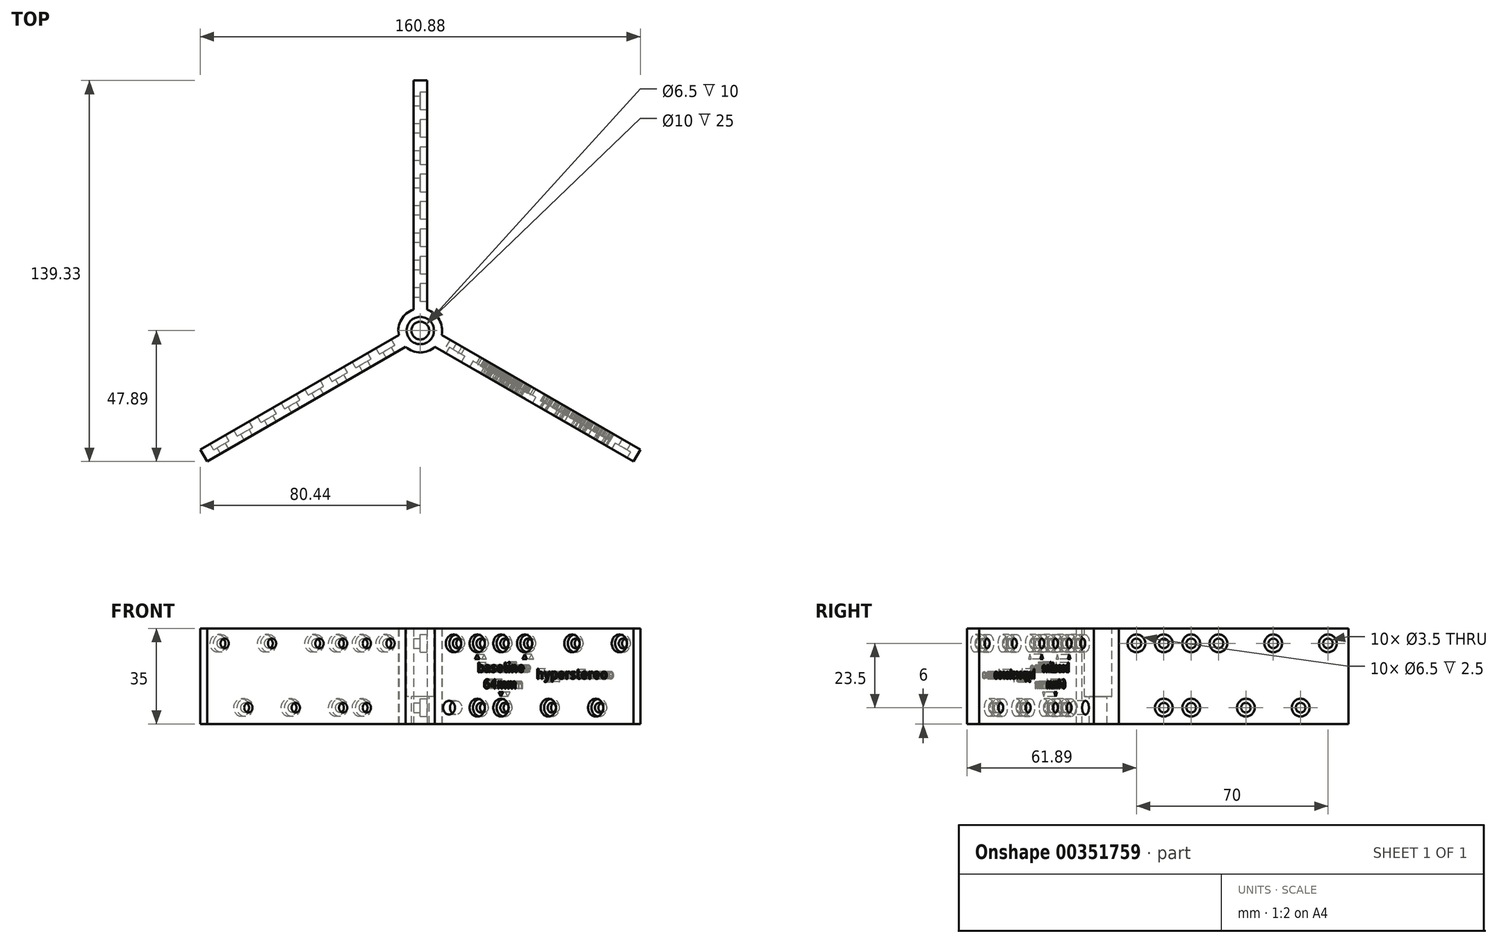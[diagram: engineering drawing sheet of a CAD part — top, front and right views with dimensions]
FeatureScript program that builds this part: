
annotation { "Feature Type Name" : "Feature", "Feature Type Description" : "" }
export const myFeature = defineFeature(function(context is Context, id is Id, definition is map)
    precondition{}
    {
        {
            var Q0;
            Q0=qCreatedBy(makeId("Top.planeOp"),FACE);
            var sketch = newSketch(context, id + "F0", { "sketchPlane" : qUnion([Q0])});
            skCircle(sketch, "E0.cCircle", {"center": v(0, 0) * mm, "radius": 1.44 * mm, "construction": true});
            skLineSegment(sketch, "E0.0", {"start": v(-2.5, 1.44) * mm, "end": v(2.5, 1.44) * mm});
            skLineSegment(sketch, "E0.1", {"start": v(2.5, 1.44) * mm, "end": v(0, -2.89) * mm});
            skLineSegment(sketch, "E0.2", {"start": v(0, -2.89) * mm, "end": v(-2.5, 1.44) * mm});
            skPoint(sketch, "E0.0.midPoint", {"position": v(0, 1.44) * mm});
            skLineSegment(sketch, "E1.top", {"start": v(-2.5, 91.44) * mm, "end": v(2.5, 91.44) * mm});
            skLineSegment(sketch, "E1.left", {"start": v(-2.5, 1.44) * mm, "end": v(-2.5, 91.44) * mm});
            skLineSegment(sketch, "E1.right", {"start": v(2.5, 1.44) * mm, "end": v(2.5, 91.44) * mm});
            skLineSegment(sketch, "E2.1.0", {"start": v(-2.5, 1.44) * mm, "end": v(-80.44, -43.56) * mm});
            skLineSegment(sketch, "E2.1.1", {"start": v(0, -2.89) * mm, "end": v(-77.94, -47.89) * mm});
            skLineSegment(sketch, "E2.1.2", {"start": v(-77.94, -47.89) * mm, "end": v(-80.44, -43.56) * mm});
            skLineSegment(sketch, "E2.2.0", {"start": v(0, -2.89) * mm, "end": v(77.94, -47.89) * mm});
            skLineSegment(sketch, "E2.2.1", {"start": v(2.5, 1.44) * mm, "end": v(80.44, -43.56) * mm});
            skLineSegment(sketch, "E2.2.2", {"start": v(80.44, -43.56) * mm, "end": v(77.94, -47.89) * mm});
            skCircle(sketch, "E3", {"center": v(0, 0) * mm, "radius": 8 * mm});
            skSolve(sketch);
        }
        {
            var Q0;
            {var subQ0=sQuery(id+"F0.wireOp",EDGE,"E0.0");Q0=makeQuery(id+"F0.imprint","IMPRINT",FACE,{"disambiguationData":[TD([[makeQuery(id+"F0.imprint","IMPRINT",EDGE,{"derivedFrom":subQ0}),1.0]])]});}
            var Q1;
            {var subQ0=sQuery(id+"F0.wireOp",EDGE,"E1.top");Q1=makeQuery(id+"F0.imprint","IMPRINT",FACE,{"disambiguationData":[TD([[makeQuery(id+"F0.imprint","IMPRINT",EDGE,{"derivedFrom":subQ0}),-1.0]])]});}
            var Q2;
            {var subQ0=sQuery(id+"F0.wireOp",EDGE,"E0.1");Q2=makeQuery(id+"F0.imprint","IMPRINT",FACE,{"disambiguationData":[TD([[makeQuery(id+"F0.imprint","IMPRINT",EDGE,{"derivedFrom":subQ0}),1.0]])]});}
            var Q3;
            Q3=makeQuery(id+"F0.imprint","IMPRINT",FACE,{"disambiguationData":[TD([[makeQuery(id+"F0.imprint","IMPRINT",EDGE,{"derivedFrom":sQuery(id+"F0.wireOp",EDGE,"E0.0")}),-1.0]])]});
            var Q4;
            {var subQ0=sQuery(id+"F0.wireOp",EDGE,"E0.2");Q4=makeQuery(id+"F0.imprint","IMPRINT",FACE,{"disambiguationData":[TD([[makeQuery(id+"F0.imprint","IMPRINT",EDGE,{"derivedFrom":subQ0}),1.0]])]});}
            var Q5;
            {var subQ3=sQuery(id+"F0.wireOp",EDGE,"E2.2.2");Q5=makeQuery(id+"F0.imprint","IMPRINT",FACE,{"disambiguationData":[TD([[makeQuery(id+"F0.imprint","IMPRINT",EDGE,{"derivedFrom":subQ3}),-1.0]])]});}
            var Q6;
            {var subQ3=sQuery(id+"F0.wireOp",EDGE,"E2.1.2");Q6=makeQuery(id+"F0.imprint","IMPRINT",FACE,{"disambiguationData":[TD([[makeQuery(id+"F0.imprint","IMPRINT",EDGE,{"derivedFrom":subQ3}),-1.0]])]});}
            extrude(context, id + "F1", {"entities" : qUnion([Q0, Q1, Q2, Q3, Q4, Q5, Q6]), "depth" : 35 * mm, "offsetDistance" : 25 * mm});
        }
        {
            var Q0;
            {var subQ1=sQuery(id+"F0.wireOp",EDGE,"E1.left");var subQ3=sQuery(id+"F0.wireOp",EDGE,"E3");var subQ4=makeQuery(id+"F0.imprint","INTERSECT",VERTEX,{"derivedFrom":[subQ1,subQ3]});Q0=makeQuery(id+"F0.imprint","IMPRINT",FACE,{"disambiguationData":[TD([[makeQuery(id+"F0.imprint","IMPRINT",EDGE,{"disambiguationData":[TD([[subQ4,-1.0]])],"derivedFrom":subQ3}),1.0]])]});}
            var Q1;
            {var subQ1=sQuery(id+"F0.wireOp",EDGE,"E1.right");var subQ3=sQuery(id+"F0.wireOp",EDGE,"E3");var subQ4=makeQuery(id+"F0.imprint","INTERSECT",VERTEX,{"derivedFrom":[subQ1,subQ3]});Q1=makeQuery(id+"F0.imprint","IMPRINT",FACE,{"disambiguationData":[TD([[makeQuery(id+"F0.imprint","IMPRINT",EDGE,{"disambiguationData":[TD([[subQ4,1.0]])],"derivedFrom":subQ3}),1.0]])]});}
            var Q2;
            {var subQ1=sQuery(id+"F0.wireOp",EDGE,"E2.1.1");var subQ3=sQuery(id+"F0.wireOp",EDGE,"E3");var subQ4=makeQuery(id+"F0.imprint","INTERSECT",VERTEX,{"derivedFrom":[subQ1,subQ3]});Q2=makeQuery(id+"F0.imprint","IMPRINT",FACE,{"disambiguationData":[TD([[makeQuery(id+"F0.imprint","IMPRINT",EDGE,{"disambiguationData":[TD([[subQ4,-1.0]])],"derivedFrom":subQ3}),1.0]])]});}
            extrude(context, id + "F2", {"entities" : qUnion([Q0, Q1, Q2]), "operationType" : NewBodyOperationType.ADD, "depth" : 35 * mm, "offsetDistance" : 25 * mm});
        }
        {
            var Q0;
            Q0=makeQuery(id+"F1.opExtrude","SWEPT_FACE",FACE,{"disambiguationData":[OSD([sQuery(id+"F0.wireOp",EDGE,"E2.2.0")])]});
            var sketch = newSketch(context, id + "F3", { "sketchPlane" : qUnion([Q0])});
            skCircle(sketch, "E4", {"center": v(25.5, 29.5) * mm, "radius": 4.05 * mm});
            skCircle(sketch, "E5", {"center": v(45.5, 29.5) * mm, "radius": 3.1 * mm});
            skCircle(sketch, "E6", {"center": v(35.5, 6) * mm, "radius": 2.81 * mm});
            skCircle(sketch, "E7", {"center": v(13.6, 6) * mm, "radius": 2.5 * mm});
            skCircle(sketch, "E8", {"center": v(65.5, 29.5) * mm, "radius": 3.27 * mm});
            skCircle(sketch, "E9", {"center": v(55.5, 6) * mm, "radius": 2.89 * mm});
            skCircle(sketch, "E10", {"center": v(85.5, 29.5) * mm, "radius": 3 * mm});
            skCircle(sketch, "E11", {"center": v(75.5, 6) * mm, "radius": 3.61 * mm});
            skCircle(sketch, "E12", {"center": v(35.5, 29.5) * mm, "radius": 2.46 * mm});
            skCircle(sketch, "E13", {"center": v(15.5, 29.5) * mm, "radius": 2.54 * mm});
            skCircle(sketch, "E14", {"center": v(25.5, 6) * mm, "radius": 2.1 * mm});
            skCircle(sketch, "E15.cCircle", {"center": v(25.5, 24.35) * mm, "radius": 0.58 * mm, "construction": true});
            skLineSegment(sketch, "E15.0", {"start": v(26.5, 23.77) * mm, "end": v(24.5, 23.77) * mm});
            skLineSegment(sketch, "E15.1", {"start": v(24.5, 23.77) * mm, "end": v(25.5, 25.5) * mm});
            skLineSegment(sketch, "E15.2", {"start": v(25.5, 25.5) * mm, "end": v(26.5, 23.77) * mm});
            skPoint(sketch, "E15.0.midPoint", {"position": v(25.5, 23.77) * mm});
            skCircle(sketch, "E16.cCircle", {"center": v(45.5, 24.35) * mm, "radius": 0.58 * mm, "construction": true});
            skLineSegment(sketch, "E16.0", {"start": v(46.5, 23.77) * mm, "end": v(44.5, 23.77) * mm});
            skLineSegment(sketch, "E16.1", {"start": v(44.5, 23.77) * mm, "end": v(45.5, 25.5) * mm});
            skLineSegment(sketch, "E16.2", {"start": v(45.5, 25.5) * mm, "end": v(46.5, 23.77) * mm});
            skPoint(sketch, "E16.0.midPoint", {"position": v(45.5, 23.77) * mm});
            skCircle(sketch, "E17.cCircle", {"center": v(35.5, 11.15) * mm, "radius": 0.58 * mm, "construction": true});
            skLineSegment(sketch, "E17.0", {"start": v(34.5, 11.73) * mm, "end": v(36.5, 11.73) * mm});
            skLineSegment(sketch, "E17.1", {"start": v(36.5, 11.73) * mm, "end": v(35.5, 10) * mm});
            skLineSegment(sketch, "E17.2", {"start": v(35.5, 10) * mm, "end": v(34.5, 11.73) * mm});
            skPoint(sketch, "E17.0.midPoint", {"position": v(35.5, 11.73) * mm});
            skSolve(sketch);
        }
        {
            var Q0;
            Q0=makeQuery(id+"F1.opExtrude","SWEPT_FACE",FACE,{"disambiguationData":[OSD([sQuery(id+"F0.wireOp",EDGE,"E1.right")])]});
            var sketch = newSketch(context, id + "F4", { "sketchPlane" : qUnion([Q0])});
            skCircle(sketch, "E18", {"center": v(24, 29.5) * mm, "radius": 3.54 * mm});
            skCircle(sketch, "E19", {"center": v(44, 29.5) * mm, "radius": 6.4 * mm});
            skCircle(sketch, "E20", {"center": v(34, 6) * mm, "radius": 7.3 * mm});
            skCircle(sketch, "E21", {"center": v(64, 29.5) * mm, "radius": 3.8 * mm});
            skCircle(sketch, "E22", {"center": v(84, 29.5) * mm, "radius": 3.17 * mm});
            skCircle(sketch, "E23", {"center": v(54, 6) * mm, "radius": 4.07 * mm});
            skCircle(sketch, "E24", {"center": v(74, 6) * mm, "radius": 4 * mm});
            skCircle(sketch, "E25", {"center": v(34, 29.5) * mm, "radius": 2.4 * mm});
            skCircle(sketch, "E26", {"center": v(14, 29.5) * mm, "radius": 2.41 * mm});
            skCircle(sketch, "E27", {"center": v(24, 6) * mm, "radius": 2.23 * mm});
            skSolve(sketch);
        }
        {
            var Q0;
            Q0=makeQuery(id+"F1.opExtrude","SWEPT_FACE",FACE,{"disambiguationData":[OSD([sQuery(id+"F0.wireOp",EDGE,"E2.1.0")])]});
            var sketch = newSketch(context, id + "F5", { "sketchPlane" : qUnion([Q0])});
            skCircle(sketch, "E28", {"center": v(24, 29.5) * mm, "radius": 4.06 * mm});
            skCircle(sketch, "E29", {"center": v(44, 29.5) * mm, "radius": 3.4 * mm});
            skCircle(sketch, "E30", {"center": v(34, 6) * mm, "radius": 3.73 * mm});
            skCircle(sketch, "E31", {"center": v(64, 29.5) * mm, "radius": 3.27 * mm});
            skCircle(sketch, "E32", {"center": v(84, 29.5) * mm, "radius": 3.9 * mm});
            skCircle(sketch, "E33", {"center": v(54, 6) * mm, "radius": 2.56 * mm});
            skCircle(sketch, "E34", {"center": v(74, 6) * mm, "radius": 2.6 * mm});
            skCircle(sketch, "E35", {"center": v(34, 29.5) * mm, "radius": 2.03 * mm});
            skCircle(sketch, "E36", {"center": v(14, 29.5) * mm, "radius": 2.7 * mm});
            skCircle(sketch, "E37", {"center": v(24, 6) * mm, "radius": 2.1 * mm});
            skSolve(sketch);
        }
        {
            var Q0;
            Q0=sQuery(id+"F3.wireOp",VERTEX,"E4.center");
            var Q1;
            Q1=sQuery(id+"F3.wireOp",VERTEX,"E5.center");
            var Q2;
            Q2=sQuery(id+"F3.wireOp",VERTEX,"E6.center");
            var Q3;
            Q3=sQuery(id+"F3.wireOp",VERTEX,"J4H1sDij-j8pw-lzHa-J71y-kKgUzP2udfqF.center");
            var Q4;
            Q4=sQuery(id+"F3.wireOp",VERTEX,"WJUUoE4I-0MqD-CSnc-YH1T-ajHH5fHvrCzP.center");
            var Q5;
            Q5=sQuery(id+"F3.wireOp",VERTEX,"r6gi781G-hVcB-m9MC-abQT-lkCxCSLe8G7L.center");
            var Q6;
            Q6=sQuery(id+"F3.wireOp",VERTEX,"E8.center");
            var Q7;
            Q7=sQuery(id+"F3.wireOp",VERTEX,"E9.center");
            var Q8;
            Q8=sQuery(id+"F3.wireOp",VERTEX,"E10.center");
            var Q9;
            Q9=sQuery(id+"F3.wireOp",VERTEX,"E11.center");
            var Q10;
            Q10=sQuery(id+"F3.wireOp",VERTEX,"E12.center");
            var Q11;
            Q11=sQuery(id+"F3.wireOp",VERTEX,"E13.center");
            var Q12;
            Q12=sQuery(id+"F3.wireOp",VERTEX,"E14.center");
            var Q13;
            Q13=makeQuery(id+"F1.opExtrude","SWEPT_BODY",BODY,{"disambiguationData":[OSD([sQuery(id+"F0.wireOp",EDGE,"E1.top"),sQuery(id+"F0.wireOp",EDGE,"E1.left"),sQuery(id+"F0.wireOp",EDGE,"E1.right"),sQuery(id+"F0.wireOp",EDGE,"E2.1.0"),sQuery(id+"F0.wireOp",EDGE,"E2.1.1"),sQuery(id+"F0.wireOp",EDGE,"E2.1.2"),sQuery(id+"F0.wireOp",EDGE,"E2.2.0"),sQuery(id+"F0.wireOp",EDGE,"E2.2.1"),sQuery(id+"F0.wireOp",EDGE,"E2.2.2")])]});
            hole(context, id + "F6", {"style" : HoleStyle.C_BORE, "endStyle" : HoleEndStyle.BLIND, "holeDiameter" : 3.5 * mm, "cBoreDiameter" : 6.5 * mm, "cBoreDepth" : 2.5 * mm, "majorDiameter" : 5 * mm, "holeDepth" : 12 * mm, "isTappedThrough" : true, "tappedDepth" : 12 * mm, "tapClearance" : 3, "locations" : qUnion([Q0, Q1, Q2, Q3, Q4, Q5, Q6, Q7, Q8, Q9, Q10, Q11, Q12]), "scope" : qUnion([Q13])});
        }
        {
            var Q0;
            Q0=sQuery(id+"F4.wireOp",VERTEX,"E18.center");
            var Q1;
            Q1=sQuery(id+"F4.wireOp",VERTEX,"E19.center");
            var Q2;
            Q2=sQuery(id+"F4.wireOp",VERTEX,"E20.center");
            var Q3;
            Q3=sQuery(id+"F4.wireOp",VERTEX,"E21.center");
            var Q4;
            Q4=sQuery(id+"F4.wireOp",VERTEX,"E23.center");
            var Q5;
            Q5=sQuery(id+"F4.wireOp",VERTEX,"E24.center");
            var Q6;
            Q6=sQuery(id+"F4.wireOp",VERTEX,"E22.center");
            var Q7;
            Q7=sQuery(id+"F4.wireOp",VERTEX,"E26.center");
            var Q8;
            Q8=sQuery(id+"F4.wireOp",VERTEX,"E25.center");
            var Q9;
            Q9=sQuery(id+"F4.wireOp",VERTEX,"E27.center");
            var Q10;
            Q10=makeQuery(id+"F1.opExtrude","SWEPT_BODY",BODY,{"disambiguationData":[OSD([sQuery(id+"F0.wireOp",EDGE,"E1.top"),sQuery(id+"F0.wireOp",EDGE,"E1.left"),sQuery(id+"F0.wireOp",EDGE,"E1.right"),sQuery(id+"F0.wireOp",EDGE,"E2.1.0"),sQuery(id+"F0.wireOp",EDGE,"E2.1.1"),sQuery(id+"F0.wireOp",EDGE,"E2.1.2"),sQuery(id+"F0.wireOp",EDGE,"E2.2.0"),sQuery(id+"F0.wireOp",EDGE,"E2.2.1"),sQuery(id+"F0.wireOp",EDGE,"E2.2.2")])]});
            hole(context, id + "F7", {"style" : HoleStyle.C_BORE, "endStyle" : HoleEndStyle.BLIND, "holeDiameter" : 3.5 * mm, "cBoreDiameter" : 6.5 * mm, "cBoreDepth" : 2.5 * mm, "majorDiameter" : 5 * mm, "holeDepth" : 12 * mm, "isTappedThrough" : true, "tappedDepth" : 12 * mm, "tapClearance" : 3, "locations" : qUnion([Q0, Q1, Q2, Q3, Q4, Q5, Q6, Q7, Q8, Q9]), "scope" : qUnion([Q10])});
        }
        {
            var Q0;
            Q0=sQuery(id+"F5.wireOp",VERTEX,"E28.center");
            var Q1;
            Q1=sQuery(id+"F5.wireOp",VERTEX,"E29.center");
            var Q2;
            Q2=sQuery(id+"F5.wireOp",VERTEX,"E30.center");
            var Q3;
            Q3=sQuery(id+"F5.wireOp",VERTEX,"E31.center");
            var Q4;
            Q4=sQuery(id+"F5.wireOp",VERTEX,"E32.center");
            var Q5;
            Q5=sQuery(id+"F5.wireOp",VERTEX,"E34.center");
            var Q6;
            Q6=sQuery(id+"F5.wireOp",VERTEX,"E33.center");
            var Q7;
            Q7=sQuery(id+"F5.wireOp",VERTEX,"E35.center");
            var Q8;
            Q8=sQuery(id+"F5.wireOp",VERTEX,"E36.center");
            var Q9;
            Q9=sQuery(id+"F5.wireOp",VERTEX,"E37.center");
            var Q10;
            Q10=makeQuery(id+"F1.opExtrude","SWEPT_BODY",BODY,{"disambiguationData":[OSD([sQuery(id+"F0.wireOp",EDGE,"E1.top"),sQuery(id+"F0.wireOp",EDGE,"E1.left"),sQuery(id+"F0.wireOp",EDGE,"E1.right"),sQuery(id+"F0.wireOp",EDGE,"E2.1.0"),sQuery(id+"F0.wireOp",EDGE,"E2.1.1"),sQuery(id+"F0.wireOp",EDGE,"E2.1.2"),sQuery(id+"F0.wireOp",EDGE,"E2.2.0"),sQuery(id+"F0.wireOp",EDGE,"E2.2.1"),sQuery(id+"F0.wireOp",EDGE,"E2.2.2")])]});
            hole(context, id + "F8", {"style" : HoleStyle.C_BORE, "endStyle" : HoleEndStyle.BLIND, "holeDiameter" : 3.5 * mm, "cBoreDiameter" : 6.5 * mm, "cBoreDepth" : 2.5 * mm, "majorDiameter" : 5 * mm, "holeDepth" : 12 * mm, "isTappedThrough" : true, "tappedDepth" : 12 * mm, "tapClearance" : 3, "locations" : qUnion([Q0, Q1, Q2, Q3, Q4, Q5, Q6, Q7, Q8, Q9]), "scope" : qUnion([Q10])});
        }
        {
            var Q0;
            Q0=makeQuery(id+"F3.imprint","IMPRINT",FACE,{"disambiguationData":[TD([[makeQuery(id+"F3.imprint","IMPRINT",EDGE,{"derivedFrom":sQuery(id+"F3.wireOp",EDGE,"E7")}),1.0]])]});
            extrude(context, id + "F9", {"entities" : qUnion([Q0]), "operationType" : NewBodyOperationType.REMOVE, "oppositeDirection" : true, "depth" : 25 * mm, "offsetDistance" : 25 * mm});
        }
        {
            var Q0;
            {var subQ0=sQuery(id+"F0.wireOp",EDGE,"E3");var subQ1=sQuery(id+"F0.wireOp",EDGE,"E2.2.0");var subQ2=sQuery(id+"F0.wireOp",EDGE,"E2.1.1");var subQ3=sQuery(id+"F0.wireOp",EDGE,"E2.2.1");var subQ4=sQuery(id+"F0.wireOp",EDGE,"E1.right");var subQ5=sQuery(id+"F0.wireOp",EDGE,"E2.1.0");var subQ6=sQuery(id+"F0.wireOp",EDGE,"E1.left");Q0=makeQuery(id+"F2.boolean.opBoolean","MERGE",FACE,{"derivedFrom":[makeQuery(id+"F1.opExtrude","CAP_FACE",FACE,{"disambiguationData":[OSD([sQuery(id+"F0.wireOp",EDGE,"E1.top"),subQ6,subQ4,subQ5,subQ2,sQuery(id+"F0.wireOp",EDGE,"E2.1.2"),subQ1,subQ3,sQuery(id+"F0.wireOp",EDGE,"E2.2.2")])],"isStart":false}),makeQuery(id+"F2.opExtrude","CAP_FACE",FACE,{"disambiguationData":[OSD([subQ6,subQ5,subQ0])],"isStart":false}),makeQuery(id+"F2.opExtrude","CAP_FACE",FACE,{"disambiguationData":[OSD([subQ4,subQ3,subQ0])],"isStart":false}),makeQuery(id+"F2.opExtrude","CAP_FACE",FACE,{"disambiguationData":[OSD([subQ2,subQ1,subQ0])],"isStart":false})]});}
            var sketch = newSketch(context, id + "F10", { "sketchPlane" : qUnion([Q0])});
            skCircle(sketch, "E38", {"center": v(0, 0) * mm, "radius": 6.4 * mm});
            skSolve(sketch);
        }
        {
            var Q0;
            Q0=sQuery(id+"F10.wireOp",VERTEX,"E38.center");
            var Q1;
            Q1=makeQuery(id+"F1.opExtrude","SWEPT_BODY",BODY,{"disambiguationData":[OSD([sQuery(id+"F0.wireOp",EDGE,"E1.top"),sQuery(id+"F0.wireOp",EDGE,"E1.left"),sQuery(id+"F0.wireOp",EDGE,"E1.right"),sQuery(id+"F0.wireOp",EDGE,"E2.1.0"),sQuery(id+"F0.wireOp",EDGE,"E2.1.1"),sQuery(id+"F0.wireOp",EDGE,"E2.1.2"),sQuery(id+"F0.wireOp",EDGE,"E2.2.0"),sQuery(id+"F0.wireOp",EDGE,"E2.2.1"),sQuery(id+"F0.wireOp",EDGE,"E2.2.2")])]});
            hole(context, id + "F11", {"style" : HoleStyle.C_BORE, "endStyle" : HoleEndStyle.BLIND, "holeDiameter" : 6.5 * mm, "cBoreDiameter" : 10 * mm, "cBoreDepth" : 25 * mm, "majorDiameter" : 5 * mm, "holeDepth" : 35 * mm, "isTappedThrough" : true, "tappedDepth" : 12 * mm, "tapClearance" : 3, "locations" : qUnion([Q0]), "scope" : qUnion([Q1])});
        }
        {
            var Q0;
            Q0=makeQuery(id+"F3.imprint","IMPRINT",FACE,{"disambiguationData":[TD([[makeQuery(id+"F3.imprint","IMPRINT",EDGE,{"derivedFrom":sQuery(id+"F3.wireOp",EDGE,"E4")}),-1.0]])]});
            var sketch = newSketch(context, id + "F12", { "sketchPlane" : qUnion([Q0])});
            skText(sketch, "E39", { "text": "baseline\n  64mm", "fontName": "AllertaStencil-Regular.ttf"});
            skText(sketch, "E40", { "text": "hyperstereo", "fontName": "AllertaStencil-Regular.ttf"});
            const initialGuessF12  = {"E39": [0.0255, 0.019, 1, 0, 0.00337], "E40": [0.0505, 0.01655, 1, 0, 0.00345]};
            skSetInitialGuess(sketch, initialGuessF12);
            skSolve(sketch);
        }
        {
            var Q0;
            Q0 = qSketchRegion(id + "F12", true);
            var Q1;
            {var subQ5=sQuery(id+"F3.wireOp",EDGE,"E15.0");Q1=makeQuery(id+"F3.imprint","IMPRINT",FACE,{"disambiguationData":[TD([[makeQuery(id+"F3.imprint","IMPRINT",EDGE,{"derivedFrom":subQ5}),-1.0]])]});}
            var Q2;
            Q2=makeQuery(id+"F3.imprint","IMPRINT",FACE,{"disambiguationData":[TD([[makeQuery(id+"F3.imprint","IMPRINT",EDGE,{"derivedFrom":sQuery(id+"F3.wireOp",EDGE,"E16.0")}),-1.0]])]});
            var Q3;
            Q3=makeQuery(id+"F3.imprint","IMPRINT",FACE,{"disambiguationData":[TD([[makeQuery(id+"F3.imprint","IMPRINT",EDGE,{"derivedFrom":sQuery(id+"F3.wireOp",EDGE,"E17.0")}),-1.0]])]});
            extrude(context, id + "F13", {"entities" : qUnion([Q0, Q1, Q2, Q3]), "operationType" : NewBodyOperationType.REMOVE, "oppositeDirection" : true, "depth" : 25 * mm, "offsetDistance" : 25 * mm});
        }
    });
